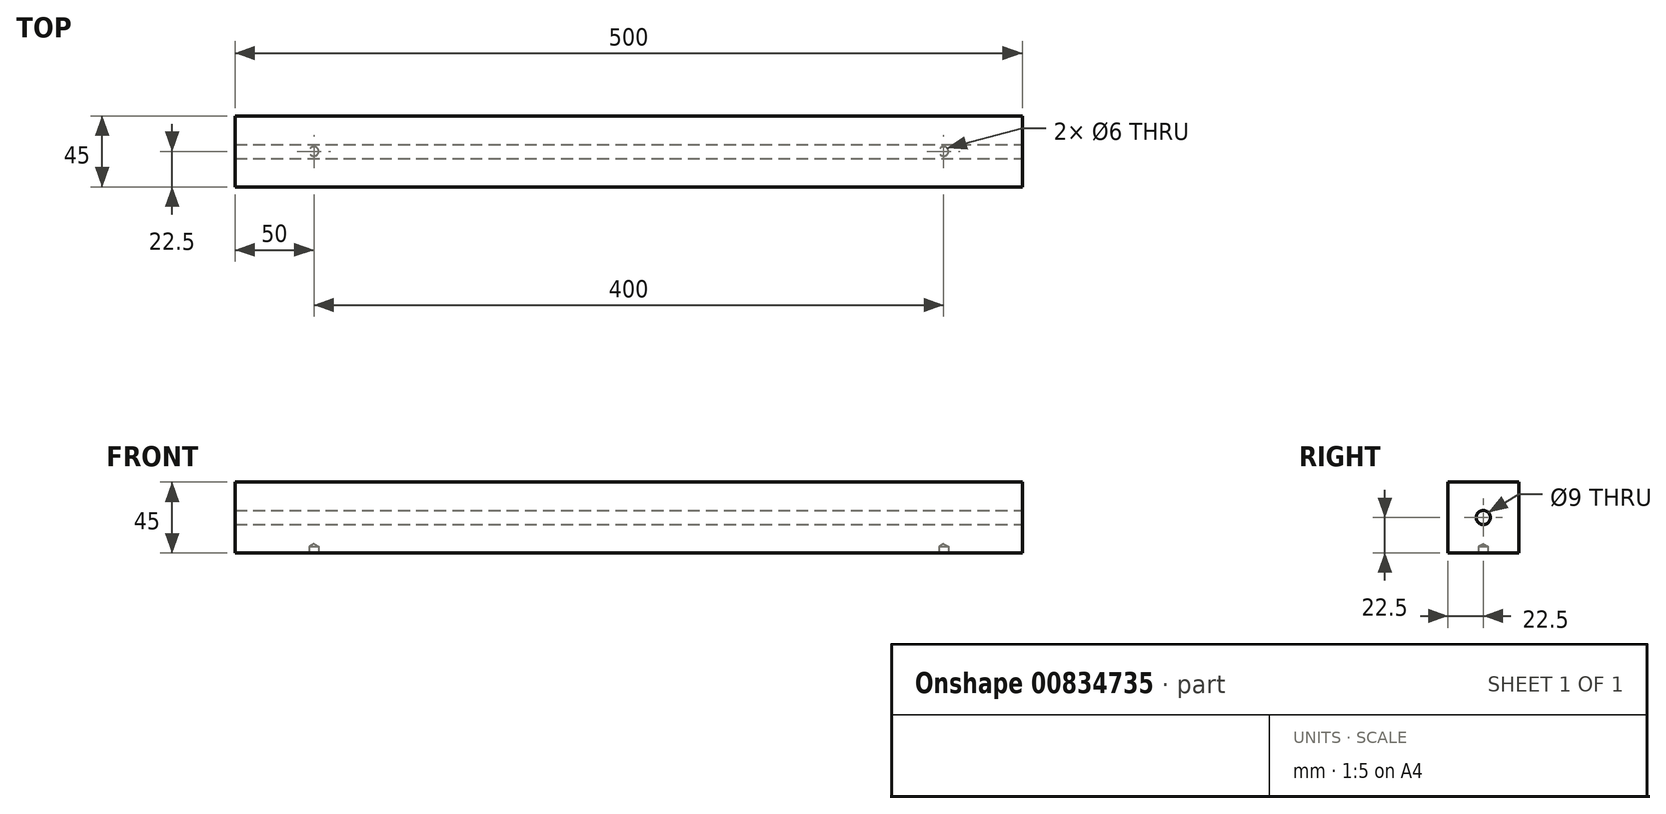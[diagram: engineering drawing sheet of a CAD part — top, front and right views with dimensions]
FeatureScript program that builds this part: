
annotation { "Feature Type Name" : "Feature", "Feature Type Description" : "" }
export const myFeature = defineFeature(function(context is Context, id is Id, definition is map)
    precondition{}
    {
        {
            var Q0;
            Q0=qCreatedBy(makeId("Right.planeOp"),FACE);
            var sketch = newSketch(context, id + "F0", { "sketchPlane" : qUnion([Q0])});
            skLineSegment(sketch, "E0.bottom", {"start": v(-22.5, 22.5) * mm, "end": v(22.5, 22.5) * mm});
            skLineSegment(sketch, "E0.top", {"start": v(-22.5, -22.5) * mm, "end": v(22.5, -22.5) * mm});
            skLineSegment(sketch, "E0.left", {"start": v(-22.5, 22.5) * mm, "end": v(-22.5, -22.5) * mm});
            skLineSegment(sketch, "E0.right", {"start": v(22.5, 22.5) * mm, "end": v(22.5, -22.5) * mm});
            skPoint(sketch, "E0.middle", {"position": v(0, 0) * mm});
            skCircle(sketch, "E1", {"center": v(0, 0) * mm, "radius": 4.5 * mm});
            skSolve(sketch);
        }
        {
            var Q0;
            Q0=makeQuery(id+"F0.imprint","IMPRINT",FACE,{"disambiguationData":[TD([[makeQuery(id+"F0.imprint","IMPRINT",EDGE,{"derivedFrom":sQuery(id+"F0.wireOp",EDGE,"E0.bottom")}),-1.0]])]});
            extrude(context, id + "F1", {"entities" : qUnion([Q0]), "oppositeDirection" : true, "depth" : 500 * mm, "offsetDistance" : 25 * mm});
        }
        {
            var Q0;
            Q0=makeQuery(id+"F1.opExtrude","SWEPT_FACE",FACE,{"disambiguationData":[OSD([sQuery(id+"F0.wireOp",EDGE,"E0.top")])]});
            var sketch = newSketch(context, id + "F2", { "sketchPlane" : qUnion([Q0])});
            skLineSegment(sketch, "E2", {"start": v(0, 0) * mm, "end": v(-500, 0) * mm});
            skPoint(sketch, "E3", {"position": v(-50, 0) * mm});
            skPoint(sketch, "E4", {"position": v(-450, 0) * mm});
            skSolve(sketch);
        }
        {
            var Q0;
            Q0=sQuery(id+"F2.wireOp",VERTEX,"E3");
            var Q1;
            Q1=sQuery(id+"F2.wireOp",VERTEX,"E4");
            var Q2;
            Q2=makeQuery(id+"F1.opExtrude","SWEPT_BODY",BODY,{"disambiguationData":[OSD([sQuery(id+"F0.wireOp",EDGE,"E0.bottom"),sQuery(id+"F0.wireOp",EDGE,"E0.top"),sQuery(id+"F0.wireOp",EDGE,"E0.left"),sQuery(id+"F0.wireOp",EDGE,"E0.right"),sQuery(id+"F0.wireOp",EDGE,"E1")])]});
            hole(context, id + "F3", {"style" : HoleStyle.SIMPLE, "endStyle" : HoleEndStyle.BLIND, "holeDiameter" : 6 * mm, "majorDiameter" : 5 * mm, "holeDepth" : 4 * mm, "isTappedThrough" : true, "tappedDepth" : 12 * mm, "tapClearance" : 3, "locations" : qUnion([Q0, Q1]), "scope" : qUnion([Q2])});
        }
    });
